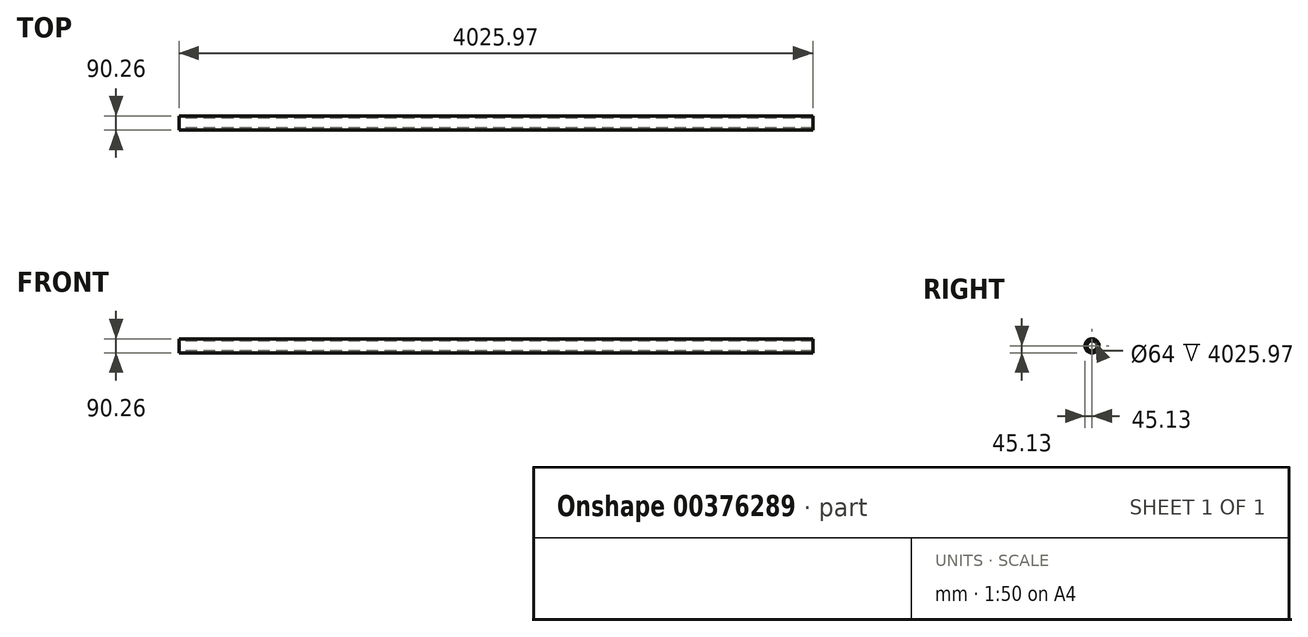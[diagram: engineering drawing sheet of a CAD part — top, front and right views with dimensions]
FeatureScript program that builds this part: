
annotation { "Feature Type Name" : "Feature", "Feature Type Description" : "" }
export const myFeature = defineFeature(function(context is Context, id is Id, definition is map)
    precondition{}
    {
        {
            var Q0;
            Q0=qCreatedBy(makeId("Right.planeOp"),FACE);
            var sketch = newSketch(context, id + "F0", { "sketchPlane" : qUnion([Q0])});
            skCircle(sketch, "E0", {"center": v(0, 0) * mm, "radius": 32 * mm});
            skCircle(sketch, "E1", {"center": v(0, 0) * mm, "radius": 45.13 * mm});
            skSolve(sketch);
        }
        {
            var Q0;
            Q0=makeQuery(id+"F0.imprint","IMPRINT",FACE,{"disambiguationData":[TD([[makeQuery(id+"F0.imprint","IMPRINT",EDGE,{"derivedFrom":sQuery(id+"F0.wireOp",EDGE,"E0")}),-1.0]])]});
            extrude(context, id + "F1", {"entities" : qUnion([Q0]), "depth" : 4025.97 * mm});
        }
    });
